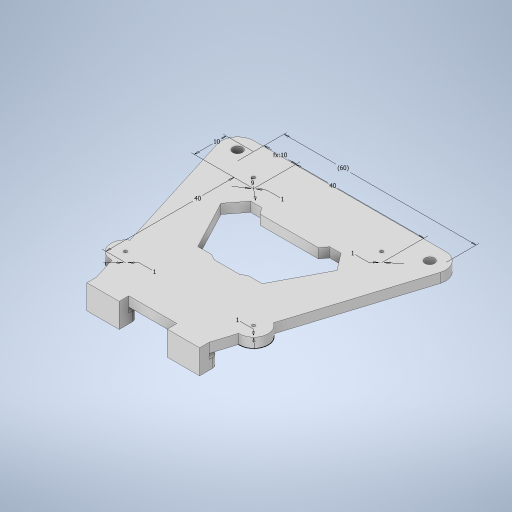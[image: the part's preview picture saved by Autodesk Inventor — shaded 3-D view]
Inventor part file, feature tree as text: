
AUTODESK INVENTOR PART (.ipt)
format: ipt  version: 2023 (Build 270158000, 158)  size: 356,864 bytes
history: native  units: in
note: dims shown in document units (in); Inventor stores cm internally (conversion verified against a paired STEP export)
features: extrude x6, sketch x5, plane x1, fillet x1
ambient origin geometry x8: Origin, YZ Plane, XZ Plane, XY Plane, X Axis, Y Axis, Z Axis, Center Point
bodies: Solid1 (feature_tree)
feature tree (13):
  extrude  "Extrusion1"  Depth=0.3976in
  extrude  "Extrusion2"  Depth=0.3976in
  plane  "Work Plane1"
  extrude  "Extrusion3"  Depth=0.3937in
  fillet  "Fillet1"  Radius=0.1181in
  sketch  "Sketch4"  dims[d7=0.1181in d8=0.1181in d9=0.0in]
  extrude  "Extrusion4"  Depth=0.1181in TaperAngle=0.0deg
  extrude  "Extrusion6"  Depth=0.1181in
  extrude  "Extrusion8"  Depth=0.1181in
  sketch  "Sketch1"  dims[d0=0.1181in d1=0.3976in]
  sketch  "Sketch2"  dims[d2=0.1181in d3=0.3976in]
  sketch  "Sketch3"  dims[d4=0.3937in d5=0.3937in d6=0.1181in]
  sketch  "Sketch6"  dims[d10=0.1811in d11=0.0in d12=0.1181in d13=0.1181in d14=0.1181in d15=0.0in d16=0.0787in d18=0.3543in d22=1.5748in d27=2.3622in d28=0.3937in d29=0.3937in d30=0.7874in d32=1.5748in d33=0.7874in d35=1.5748in d38=0.1181in d39=0.0in d43=0.3937in d44=0.0in d53=0.0394in d54=0.0394in d55=0.0394in d56=0.0394in d57=0.1181in d58=0.0in]
